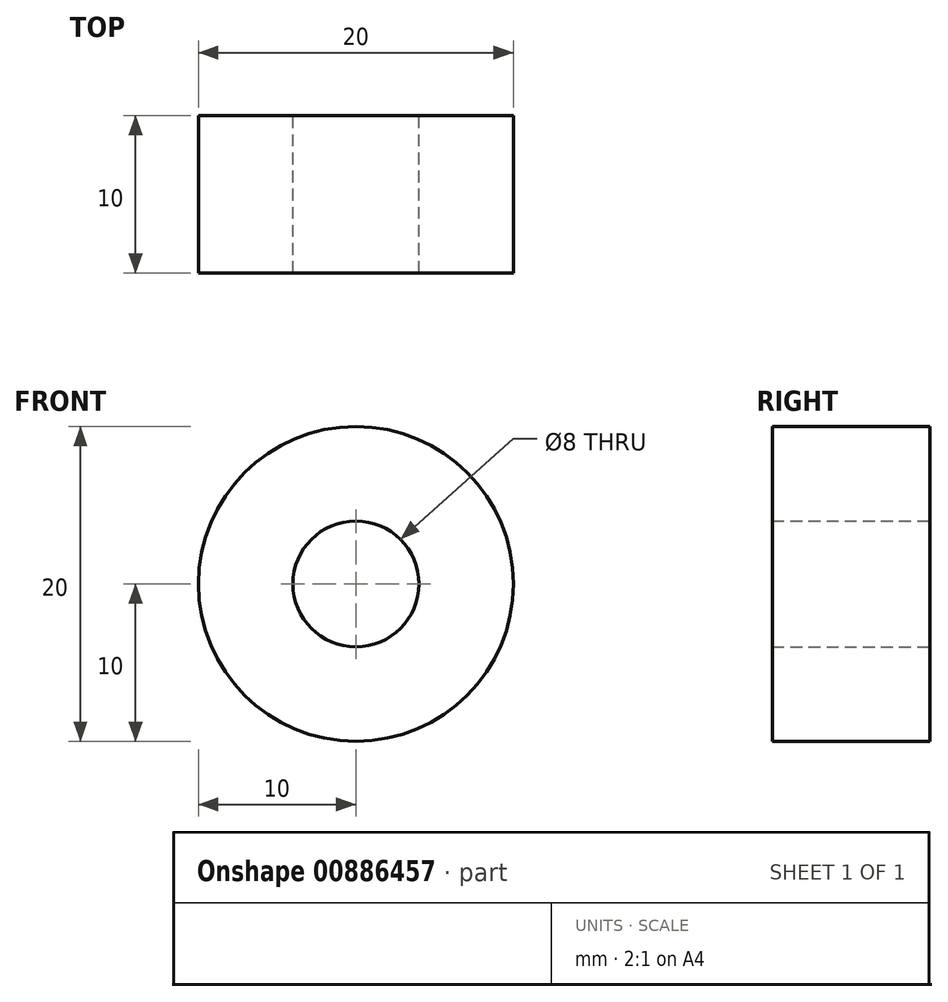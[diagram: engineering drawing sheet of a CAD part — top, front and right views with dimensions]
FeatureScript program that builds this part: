
annotation { "Feature Type Name" : "Feature", "Feature Type Description" : "" }
export const myFeature = defineFeature(function(context is Context, id is Id, definition is map)
    precondition{}
    {
        {
            var Q0;
            Q0=qCreatedBy(makeId("Front.planeOp"),FACE);
            var sketch = newSketch(context, id + "F0", { "sketchPlane" : qUnion([Q0])});
            skCircle(sketch, "E0", {"center": v(0, 0) * mm, "radius": 10 * mm});
            skCircle(sketch, "E1", {"center": v(0, 0) * mm, "radius": 4 * mm});
            skSolve(sketch);
        }
        {
            var Q0;
            Q0=makeQuery(id+"F0.imprint","IMPRINT",FACE,{"disambiguationData":[TD([[makeQuery(id+"F0.imprint","IMPRINT",EDGE,{"derivedFrom":sQuery(id+"F0.wireOp",EDGE,"E0")}),1.0]])]});
            extrude(context, id + "F1", {"entities" : qUnion([Q0]), "depth" : 10 * mm, "offsetDistance" : 25 * mm});
        }
    });
